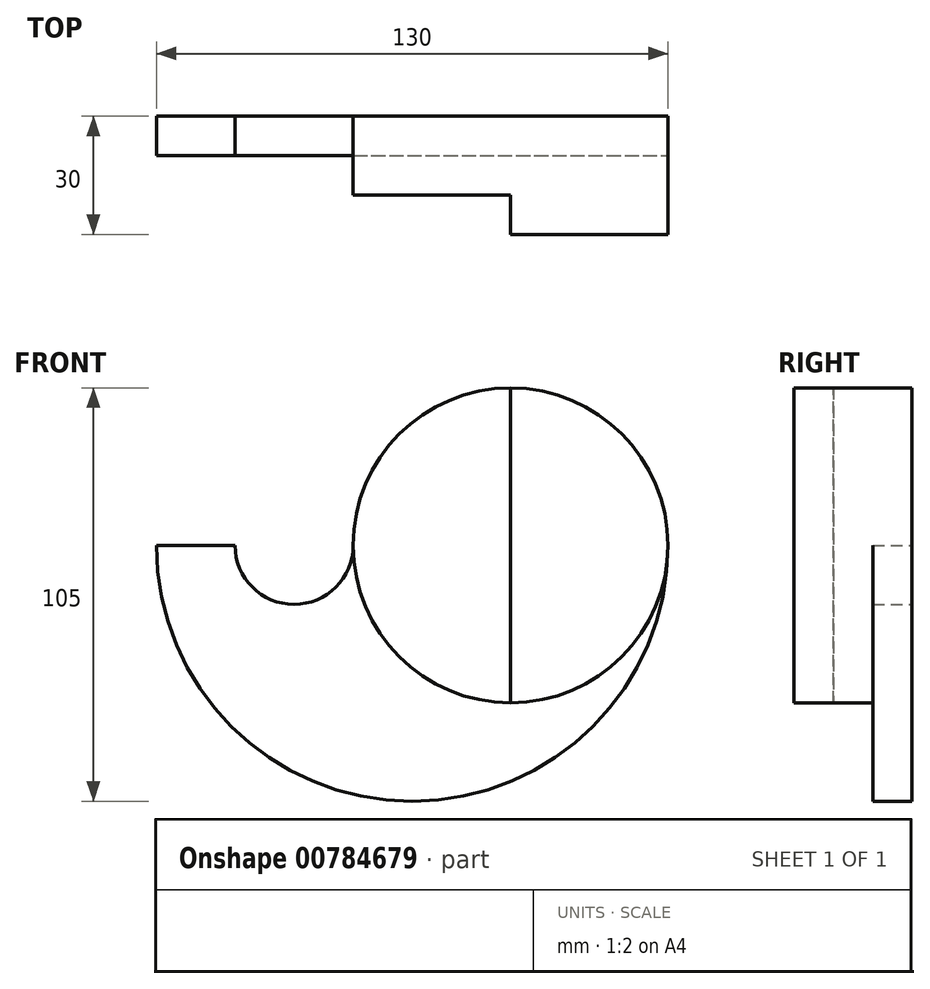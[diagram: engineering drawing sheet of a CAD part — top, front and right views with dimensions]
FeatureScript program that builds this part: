
annotation { "Feature Type Name" : "Feature", "Feature Type Description" : "" }
export const myFeature = defineFeature(function(context is Context, id is Id, definition is map)
    precondition{}
    {
        {
            var Q0;
            Q0=qCreatedBy(makeId("Front.planeOp"),FACE);
            var sketch = newSketch(context, id + "F0", { "sketchPlane" : qUnion([Q0])});
            skLineSegment(sketch, "E0", {"start": v(-65, 0) * mm, "end": v(-45, 0) * mm});
            skArc(sketch, "E1", {"start": v(-65, 0) * mm, "mid": v(0, -65) * mm, "end": v(65, 0) * mm});
            skCircle(sketch, "E2", {"center": v(25, 0) * mm, "radius": 40 * mm});
            skCircle(sketch, "E3", {"center": v(25, 0) * mm, "radius": 25 * mm});
            skArc(sketch, "E4", {"start": v(-45, 0) * mm, "mid": v(-30, -15) * mm, "end": v(-15, 0) * mm});
            skPoint(sketch, "E5.orphan", {"position": v(-105.17, 0) * mm});
            skLineSegment(sketch, "E6", {"start": v(25, 0) * mm, "end": v(25, 25) * mm});
            skLineSegment(sketch, "E7", {"start": v(25, 0) * mm, "end": v(25, -25) * mm});
            skLineSegment(sketch, "E8", {"start": v(25, 25) * mm, "end": v(25, 40) * mm});
            skLineSegment(sketch, "E9", {"start": v(25, -25) * mm, "end": v(25, -40) * mm});
            skSolve(sketch);
        }
        {
            var Q0;
            {var subQ0=sQuery(id+"F0.wireOp",EDGE,"E6");Q0=makeQuery(id+"F0.imprint","IMPRINT",FACE,{"disambiguationData":[TD([[makeQuery(id+"F0.imprint","IMPRINT",EDGE,{"derivedFrom":subQ0}),-1.0]])]});}
            var Q1;
            {var subQ0=sQuery(id+"F0.wireOp",EDGE,"E8");Q1=makeQuery(id+"F0.imprint","IMPRINT",FACE,{"disambiguationData":[TD([[makeQuery(id+"F0.imprint","IMPRINT",EDGE,{"derivedFrom":subQ0}),-1.0]])]});}
            extrude(context, id + "F1", {"entities" : qUnion([Q0, Q1]), "depth" : 30 * mm, "offsetDistance" : 25.4 * mm});
        }
        {
            var Q0;
            {var subQ0=sQuery(id+"F0.wireOp",EDGE,"E8");Q0=makeQuery(id+"F0.imprint","IMPRINT",FACE,{"disambiguationData":[TD([[makeQuery(id+"F0.imprint","IMPRINT",EDGE,{"derivedFrom":subQ0}),1.0]])]});}
            var Q1;
            {var subQ0=sQuery(id+"F0.wireOp",EDGE,"E6");Q1=makeQuery(id+"F0.imprint","IMPRINT",FACE,{"disambiguationData":[TD([[makeQuery(id+"F0.imprint","IMPRINT",EDGE,{"derivedFrom":subQ0}),1.0]])]});}
            extrude(context, id + "F2", {"entities" : qUnion([Q0, Q1]), "operationType" : NewBodyOperationType.ADD, "depth" : 20 * mm, "offsetDistance" : 25.4 * mm});
        }
        {
            var Q0;
            Q0=makeQuery(id+"F0.imprint","IMPRINT",FACE,{"disambiguationData":[TD([[makeQuery(id+"F0.imprint","IMPRINT",EDGE,{"derivedFrom":sQuery(id+"F0.wireOp",EDGE,"E0")}),-1.0]])]});
            extrude(context, id + "F3", {"entities" : qUnion([Q0]), "operationType" : NewBodyOperationType.ADD, "depth" : 10 * mm, "offsetDistance" : 25.4 * mm});
        }
    });
